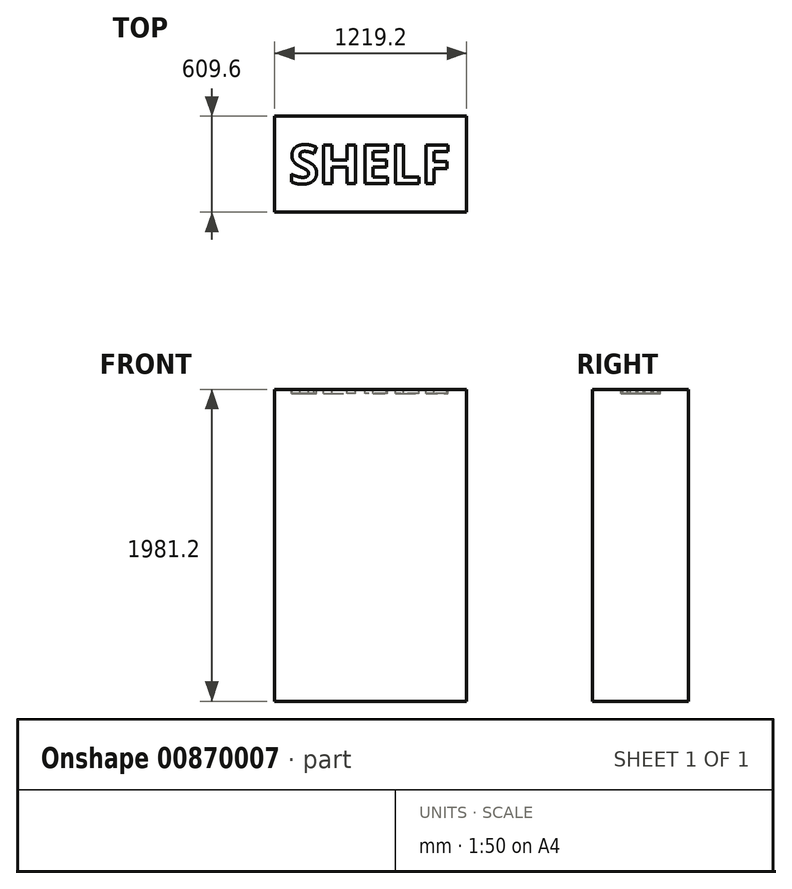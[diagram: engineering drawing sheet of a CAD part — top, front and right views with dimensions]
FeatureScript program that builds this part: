
annotation { "Feature Type Name" : "Feature", "Feature Type Description" : "" }
export const myFeature = defineFeature(function(context is Context, id is Id, definition is map)
    precondition{}
    {
        {
            var Q0;
            Q0=qCreatedBy(makeId("Top.planeOp"),FACE);
            var sketch = newSketch(context, id + "F0", { "sketchPlane" : qUnion([Q0])});
            skLineSegment(sketch, "E0.bottom", {"start": v(0, 0) * mm, "end": v(1219.2, 0) * mm});
            skLineSegment(sketch, "E0.top", {"start": v(0, 609.6) * mm, "end": v(1219.2, 609.6) * mm});
            skLineSegment(sketch, "E0.left", {"start": v(0, 0) * mm, "end": v(0, 609.6) * mm});
            skLineSegment(sketch, "E0.right", {"start": v(1219.2, 0) * mm, "end": v(1219.2, 609.6) * mm});
            skSolve(sketch);
        }
        {
            var Q0;
            Q0 = qSketchRegion(id + "F0", true);
            extrude(context, id + "F1", {"entities" : qUnion([Q0]), "depth" : 1981.2 * mm, "offsetDistance" : 25.4 * mm});
        }
        {
            var Q0;
            Q0=makeQuery(id+"F1.opExtrude","CAP_FACE",FACE,{"disambiguationData":[OSD([sQuery(id+"F0.wireOp",EDGE,"E0.bottom"),sQuery(id+"F0.wireOp",EDGE,"E0.top"),sQuery(id+"F0.wireOp",EDGE,"E0.left"),sQuery(id+"F0.wireOp",EDGE,"E0.right")])],"isStart":false});
            var sketch = newSketch(context, id + "F2", { "sketchPlane" : qUnion([Q0])});
            skText(sketch, "E1", { "text": "SHELF", "fontName": "OpenSans-Bold.ttf"});
            const initialGuessF2  = {"E1": [0.08989, 0.18145, 1, 0, 0.24756]};
            skSetInitialGuess(sketch, initialGuessF2);
            skSolve(sketch);
        }
        {
            var Q0;
            Q0 = qSketchRegion(id + "F2", true);
            extrude(context, id + "F3", {"entities" : qUnion([Q0]), "operationType" : NewBodyOperationType.REMOVE, "oppositeDirection" : true, "depth" : 25.4 * mm, "offsetDistance" : 25.4 * mm});
        }
    });
